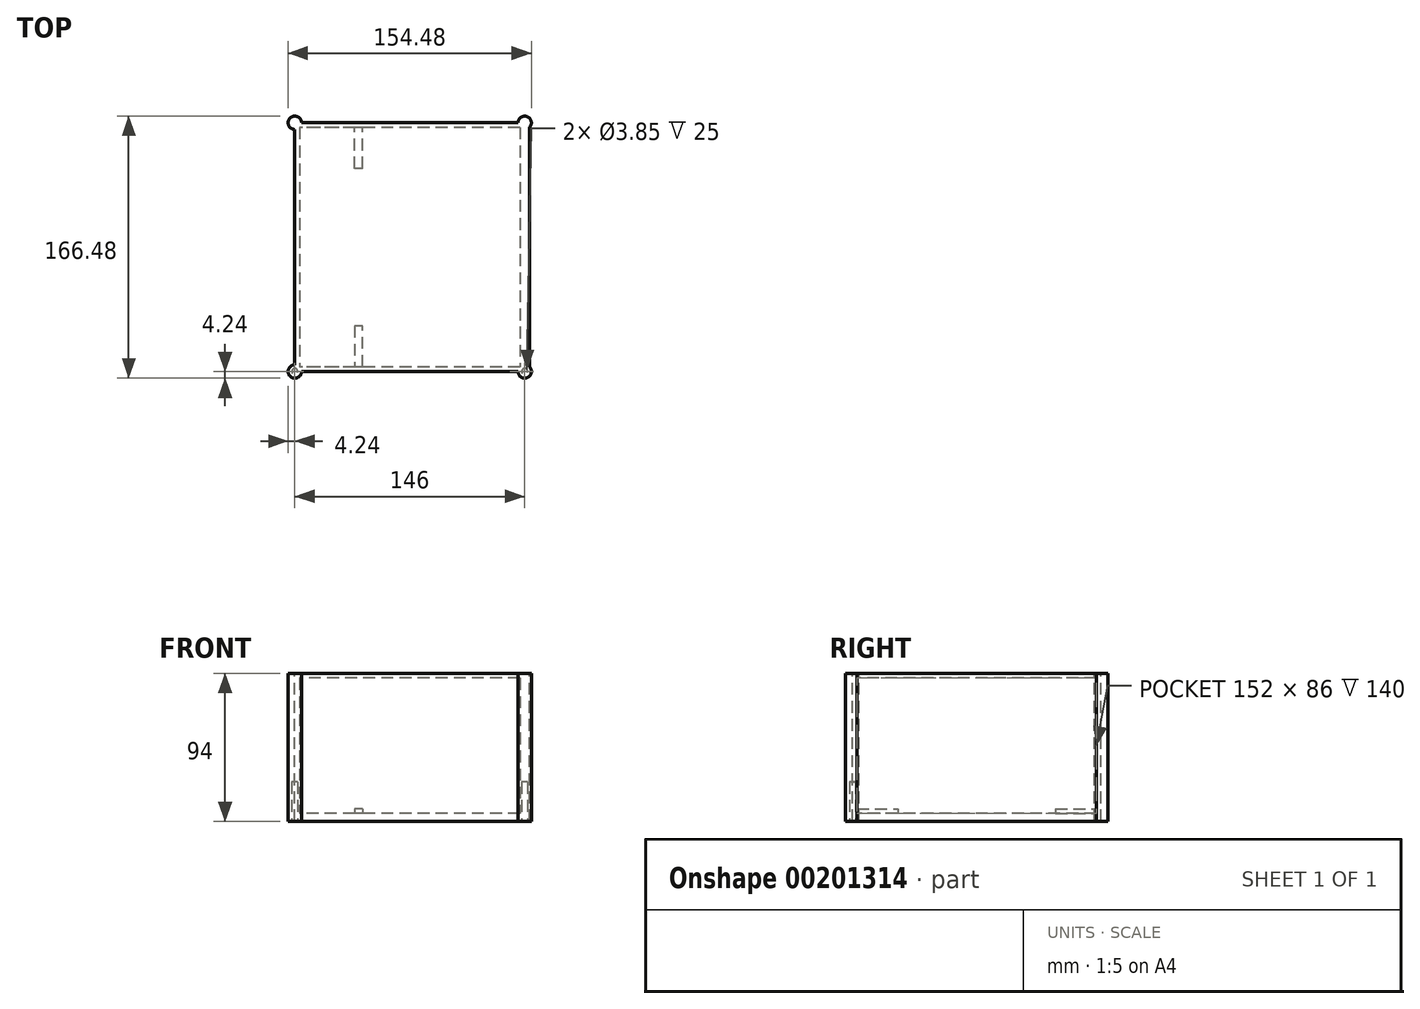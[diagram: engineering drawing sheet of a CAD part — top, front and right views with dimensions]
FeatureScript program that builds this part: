
annotation { "Feature Type Name" : "Feature", "Feature Type Description" : "" }
export const myFeature = defineFeature(function(context is Context, id is Id, definition is map)
    precondition{}
    {
        {
            var Q0;
            Q0=qCreatedBy(makeId("Top.planeOp"),FACE);
            var sketch = newSketch(context, id + "F0", { "sketchPlane" : qUnion([Q0])});
            skLineSegment(sketch, "E0.bottom", {"start": v(70, 76) * mm, "end": v(-70, 76) * mm});
            skLineSegment(sketch, "E0.top", {"start": v(70, -76) * mm, "end": v(-70, -76) * mm});
            skLineSegment(sketch, "E0.left", {"start": v(70, 76) * mm, "end": v(70, -76) * mm});
            skLineSegment(sketch, "E0.right", {"start": v(-70, 76) * mm, "end": v(-70, -76) * mm});
            skPoint(sketch, "E0.middle", {"position": v(0, 0) * mm});
            skLineSegment(sketch, "E1", {"start": v(-30, -76) * mm, "end": v(-30, 76) * mm});
            skLineSegment(sketch, "E2", {"start": v(-30, 50) * mm, "end": v(-35, 50) * mm});
            skLineSegment(sketch, "E3", {"start": v(-35, 50) * mm, "end": v(-35, 76) * mm});
            skLineSegment(sketch, "E4", {"start": v(0, 0) * mm, "end": v(70, 0) * mm, "construction": true});
            skLineSegment(sketch, "E5.MirrorCS", {"start": v(-30, -50) * mm, "end": v(-35, -50) * mm});
            skLineSegment(sketch, "E6.MirrorCS", {"start": v(-35, -50) * mm, "end": v(-35, -76) * mm});
            skLineSegment(sketch, "E7.0", {"start": v(73, 79) * mm, "end": v(73, -79) * mm});
            skLineSegment(sketch, "E7.1", {"start": v(73, 79) * mm, "end": v(-73, 79) * mm});
            skLineSegment(sketch, "E7.2", {"start": v(-73, 79) * mm, "end": v(-73, -79) * mm});
            skLineSegment(sketch, "E7.3", {"start": v(73, -79) * mm, "end": v(-73, -79) * mm});
            skLineSegment(sketch, "E8", {"start": v(70, -76) * mm, "end": v(73, -76) * mm});
            skLineSegment(sketch, "E9", {"start": v(70, 76) * mm, "end": v(73, 76) * mm});
            skCircle(sketch, "E10", {"center": v(73, -79) * mm, "radius": 4.24 * mm});
            skCircle(sketch, "E11", {"center": v(73, 79) * mm, "radius": 4.24 * mm});
            skCircle(sketch, "E12", {"center": v(-73, -79) * mm, "radius": 4.24 * mm});
            skCircle(sketch, "E13.MirrorC", {"center": v(-73, 79) * mm, "radius": 4.24 * mm});
            skSolve(sketch);
        }
        {
            var Q0;
            {var subQ1=sQuery(id+"F0.wireOp",EDGE,"E0.left");Q0=makeQuery(id+"F0.imprint","IMPRINT",FACE,{"disambiguationData":[TD([[makeQuery(id+"F0.imprint","IMPRINT",EDGE,{"derivedFrom":subQ1}),1.0]])]});}
            var Q1;
            {var subQ4=sQuery(id+"F0.wireOp",EDGE,"E0.left");Q1=makeQuery(id+"F0.imprint","IMPRINT",FACE,{"disambiguationData":[TD([[makeQuery(id+"F0.imprint","IMPRINT",EDGE,{"derivedFrom":subQ4}),-1.0]])]});}
            var Q2;
            {var subQ3=sQuery(id+"F0.wireOp",EDGE,"E0.right");Q2=makeQuery(id+"F0.imprint","IMPRINT",FACE,{"disambiguationData":[TD([[makeQuery(id+"F0.imprint","IMPRINT",EDGE,{"derivedFrom":subQ3}),1.0]])]});}
            var Q3;
            {var subQ4=sQuery(id+"F0.wireOp",EDGE,"E5.MirrorCS");Q3=makeQuery(id+"F0.imprint","IMPRINT",FACE,{"disambiguationData":[TD([[makeQuery(id+"F0.imprint","IMPRINT",EDGE,{"derivedFrom":subQ4}),1.0]])]});}
            var Q4;
            {var subQ4=sQuery(id+"F0.wireOp",EDGE,"E2");Q4=makeQuery(id+"F0.imprint","IMPRINT",FACE,{"disambiguationData":[TD([[makeQuery(id+"F0.imprint","IMPRINT",EDGE,{"derivedFrom":subQ4}),-1.0]])]});}
            var Q5;
            {var subQ5=sQuery(id+"F0.wireOp",EDGE,"E0.right");Q5=makeQuery(id+"F0.imprint","IMPRINT",FACE,{"disambiguationData":[TD([[makeQuery(id+"F0.imprint","IMPRINT",EDGE,{"derivedFrom":subQ5}),-1.0]])]});}
            var Q6;
            {var subQ0=sQuery(id+"F0.wireOp",EDGE,"E8");Q6=makeQuery(id+"F0.imprint","IMPRINT",FACE,{"disambiguationData":[TD([[makeQuery(id+"F0.imprint","IMPRINT",EDGE,{"derivedFrom":subQ0}),1.0]])]});}
            var Q7;
            {var subQ3=sQuery(id+"F0.wireOp",EDGE,"E8");Q7=makeQuery(id+"F0.imprint","IMPRINT",FACE,{"disambiguationData":[TD([[makeQuery(id+"F0.imprint","IMPRINT",EDGE,{"derivedFrom":subQ3}),-1.0]])]});}
            var Q8;
            {var subQ0=sQuery(id+"F0.wireOp",EDGE,"E7.0");var subQ1=makeQuery(id+"F0.imprint","INTERSECT",VERTEX,{"derivedFrom":[subQ0,sQuery(id+"F0.wireOp",EDGE,"E8")]});Q8=makeQuery(id+"F0.imprint","IMPRINT",FACE,{"disambiguationData":[TD([[makeQuery(id+"F0.imprint","IMPRINT",EDGE,{"disambiguationData":[TD([[subQ1,1.0]])],"derivedFrom":subQ0}),1.0]])]});}
            var Q9;
            {var subQ0=sQuery(id+"F0.wireOp",EDGE,"E9");Q9=makeQuery(id+"F0.imprint","IMPRINT",FACE,{"disambiguationData":[TD([[makeQuery(id+"F0.imprint","IMPRINT",EDGE,{"derivedFrom":subQ0}),-1.0]])]});}
            var Q10;
            {var subQ3=sQuery(id+"F0.wireOp",EDGE,"E9");Q10=makeQuery(id+"F0.imprint","IMPRINT",FACE,{"disambiguationData":[TD([[makeQuery(id+"F0.imprint","IMPRINT",EDGE,{"derivedFrom":subQ3}),1.0]])]});}
            var Q11;
            {var subQ0=sQuery(id+"F0.wireOp",EDGE,"E7.1");var subQ1=sQuery(id+"F0.wireOp",EDGE,"E7.0");var subQ2=makeQuery(id+"F0.imprint","INTERSECT",VERTEX,{"derivedFrom":[subQ1,subQ0]});Q11=makeQuery(id+"F0.imprint","IMPRINT",FACE,{"disambiguationData":[TD([[makeQuery(id+"F0.imprint","IMPRINT",EDGE,{"disambiguationData":[TD([[subQ2,-1.0]])],"derivedFrom":subQ1}),1.0]])]});}
            var Q12;
            {var subQ0=sQuery(id+"F0.wireOp",EDGE,"E2");Q12=makeQuery(id+"F0.imprint","IMPRINT",FACE,{"disambiguationData":[TD([[makeQuery(id+"F0.imprint","IMPRINT",EDGE,{"derivedFrom":subQ0}),1.0]])]});}
            var Q13;
            {var subQ5=sQuery(id+"F0.wireOp",EDGE,"E0.bottom");var subQ6=makeQuery(id+"F0.imprint","INTERSECT",VERTEX,{"derivedFrom":[subQ5,sQuery(id+"F0.wireOp",EDGE,"E1")]});Q13=makeQuery(id+"F0.imprint","IMPRINT",FACE,{"disambiguationData":[TD([[makeQuery(id+"F0.imprint","IMPRINT",EDGE,{"disambiguationData":[TD([[subQ6,-1.0]])],"derivedFrom":subQ5}),-1.0]])]});}
            var Q14;
            {var subQ0=sQuery(id+"F0.wireOp",EDGE,"E7.2");var subQ1=sQuery(id+"F0.wireOp",EDGE,"E7.1");var subQ2=makeQuery(id+"F0.imprint","INTERSECT",VERTEX,{"derivedFrom":[subQ1,subQ0]});Q14=makeQuery(id+"F0.imprint","IMPRINT",FACE,{"disambiguationData":[TD([[makeQuery(id+"F0.imprint","IMPRINT",EDGE,{"disambiguationData":[TD([[subQ2,1.0]])],"derivedFrom":subQ1}),1.0]])]});}
            var Q15;
            {var subQ0=sQuery(id+"F0.wireOp",EDGE,"E7.2");var subQ1=sQuery(id+"F0.wireOp",EDGE,"E7.1");var subQ2=makeQuery(id+"F0.imprint","INTERSECT",VERTEX,{"derivedFrom":[subQ1,subQ0]});Q15=makeQuery(id+"F0.imprint","IMPRINT",FACE,{"disambiguationData":[TD([[makeQuery(id+"F0.imprint","IMPRINT",EDGE,{"disambiguationData":[TD([[subQ2,1.0]])],"derivedFrom":subQ1}),-1.0]])]});}
            var Q16;
            {var subQ0=sQuery(id+"F0.wireOp",EDGE,"E7.3");var subQ1=sQuery(id+"F0.wireOp",EDGE,"E7.2");var subQ2=makeQuery(id+"F0.imprint","INTERSECT",VERTEX,{"derivedFrom":[subQ1,subQ0]});Q16=makeQuery(id+"F0.imprint","IMPRINT",FACE,{"disambiguationData":[TD([[makeQuery(id+"F0.imprint","IMPRINT",EDGE,{"disambiguationData":[TD([[subQ2,1.0]])],"derivedFrom":subQ1}),1.0]])]});}
            var Q17;
            {var subQ0=sQuery(id+"F0.wireOp",EDGE,"E7.3");var subQ1=sQuery(id+"F0.wireOp",EDGE,"E7.2");var subQ2=makeQuery(id+"F0.imprint","INTERSECT",VERTEX,{"derivedFrom":[subQ1,subQ0]});Q17=makeQuery(id+"F0.imprint","IMPRINT",FACE,{"disambiguationData":[TD([[makeQuery(id+"F0.imprint","IMPRINT",EDGE,{"disambiguationData":[TD([[subQ2,1.0]])],"derivedFrom":subQ1}),-1.0]])]});}
            var Q18;
            {var subQ5=sQuery(id+"F0.wireOp",EDGE,"E0.top");var subQ8=makeQuery(id+"F0.imprint","INTERSECT",VERTEX,{"derivedFrom":[subQ5,sQuery(id+"F0.wireOp",EDGE,"E1")]});Q18=makeQuery(id+"F0.imprint","IMPRINT",FACE,{"disambiguationData":[TD([[makeQuery(id+"F0.imprint","IMPRINT",EDGE,{"disambiguationData":[TD([[subQ8,-1.0]])],"derivedFrom":subQ5}),1.0]])]});}
            extrude(context, id + "F1", {"entities" : qUnion([Q0, Q1, Q2, Q3, Q4, Q5, Q6, Q7, Q8, Q9, Q10, Q11, Q12, Q13, Q14, Q15, Q16, Q17, Q18]), "oppositeDirection" : true, "depth" : 5 * mm});
        }
        {
            var Q0;
            Q0=makeQuery(id+"F0.imprint","IMPRINT",FACE,{"disambiguationData":[TD([[makeQuery(id+"F0.imprint","IMPRINT",EDGE,{"derivedFrom":sQuery(id+"F0.wireOp",EDGE,"E0.left")}),1.0]])]});
            extrude(context, id + "F2", {"entities" : qUnion([Q0]), "operationType" : NewBodyOperationType.ADD, "depth" : 86 * mm});
        }
        {
            var Q0;
            {var subQ4=sQuery(id+"F0.wireOp",EDGE,"E2");Q0=makeQuery(id+"F0.imprint","IMPRINT",FACE,{"disambiguationData":[TD([[makeQuery(id+"F0.imprint","IMPRINT",EDGE,{"derivedFrom":subQ4}),-1.0]])]});}
            var Q1;
            {var subQ4=sQuery(id+"F0.wireOp",EDGE,"E5.MirrorCS");Q1=makeQuery(id+"F0.imprint","IMPRINT",FACE,{"disambiguationData":[TD([[makeQuery(id+"F0.imprint","IMPRINT",EDGE,{"derivedFrom":subQ4}),1.0]])]});}
            extrude(context, id + "F3", {"entities" : qUnion([Q0, Q1]), "operationType" : NewBodyOperationType.ADD, "depth" : 3 * mm});
        }
        {
            var Q0;
            {var subQ5=sQuery(id+"F0.wireOp",EDGE,"E0.right");Q0=makeQuery(id+"F0.imprint","IMPRINT",FACE,{"disambiguationData":[TD([[makeQuery(id+"F0.imprint","IMPRINT",EDGE,{"derivedFrom":subQ5}),-1.0]])]});}
            var Q1;
            {var subQ3=sQuery(id+"F0.wireOp",EDGE,"E8");Q1=makeQuery(id+"F0.imprint","IMPRINT",FACE,{"disambiguationData":[TD([[makeQuery(id+"F0.imprint","IMPRINT",EDGE,{"derivedFrom":subQ3}),-1.0]])]});}
            var Q2;
            {var subQ3=sQuery(id+"F0.wireOp",EDGE,"E9");Q2=makeQuery(id+"F0.imprint","IMPRINT",FACE,{"disambiguationData":[TD([[makeQuery(id+"F0.imprint","IMPRINT",EDGE,{"derivedFrom":subQ3}),1.0]])]});}
            var Q3;
            {var subQ0=sQuery(id+"F0.wireOp",EDGE,"E7.1");var subQ1=sQuery(id+"F0.wireOp",EDGE,"E7.0");var subQ2=makeQuery(id+"F0.imprint","INTERSECT",VERTEX,{"derivedFrom":[subQ1,subQ0]});Q3=makeQuery(id+"F0.imprint","IMPRINT",FACE,{"disambiguationData":[TD([[makeQuery(id+"F0.imprint","IMPRINT",EDGE,{"disambiguationData":[TD([[subQ2,-1.0]])],"derivedFrom":subQ1}),1.0]])]});}
            var Q4;
            {var subQ0=sQuery(id+"F0.wireOp",EDGE,"E7.0");var subQ1=makeQuery(id+"F0.imprint","INTERSECT",VERTEX,{"derivedFrom":[subQ0,sQuery(id+"F0.wireOp",EDGE,"E8")]});Q4=makeQuery(id+"F0.imprint","IMPRINT",FACE,{"disambiguationData":[TD([[makeQuery(id+"F0.imprint","IMPRINT",EDGE,{"disambiguationData":[TD([[subQ1,1.0]])],"derivedFrom":subQ0}),1.0]])]});}
            var Q5;
            {var subQ0=sQuery(id+"F0.wireOp",EDGE,"E8");Q5=makeQuery(id+"F0.imprint","IMPRINT",FACE,{"disambiguationData":[TD([[makeQuery(id+"F0.imprint","IMPRINT",EDGE,{"derivedFrom":subQ0}),1.0]])]});}
            var Q6;
            {var subQ0=sQuery(id+"F0.wireOp",EDGE,"E9");Q6=makeQuery(id+"F0.imprint","IMPRINT",FACE,{"disambiguationData":[TD([[makeQuery(id+"F0.imprint","IMPRINT",EDGE,{"derivedFrom":subQ0}),-1.0]])]});}
            var Q7;
            {var subQ3=sQuery(id+"F0.wireOp",EDGE,"1c2b32d9-a7ae-4baf-86f2-c4eb9871d60d0.MirrorCS");Q7=makeQuery(id+"F0.imprint","IMPRINT",FACE,{"disambiguationData":[TD([[makeQuery(id+"F0.imprint","IMPRINT",EDGE,{"derivedFrom":subQ3}),-1.0]])]});}
            var Q8;
            {var subQ3=sQuery(id+"F0.wireOp",EDGE,"xGjk17qi-ysel-hScp-d5ul-HpHYttQAmUot");Q8=makeQuery(id+"F0.imprint","IMPRINT",FACE,{"disambiguationData":[TD([[makeQuery(id+"F0.imprint","IMPRINT",EDGE,{"derivedFrom":subQ3}),1.0]])]});}
            var Q9;
            {var subQ0=sQuery(id+"F0.wireOp",EDGE,"E7.3");var subQ1=sQuery(id+"F0.wireOp",EDGE,"E7.2");var subQ2=makeQuery(id+"F0.imprint","INTERSECT",VERTEX,{"derivedFrom":[subQ1,subQ0]});Q9=makeQuery(id+"F0.imprint","IMPRINT",FACE,{"disambiguationData":[TD([[makeQuery(id+"F0.imprint","IMPRINT",EDGE,{"disambiguationData":[TD([[subQ2,1.0]])],"derivedFrom":subQ1}),1.0]])]});}
            var Q10;
            {var subQ5=sQuery(id+"F0.wireOp",EDGE,"E0.top");var subQ8=makeQuery(id+"F0.imprint","INTERSECT",VERTEX,{"derivedFrom":[subQ5,sQuery(id+"F0.wireOp",EDGE,"E1")]});Q10=makeQuery(id+"F0.imprint","IMPRINT",FACE,{"disambiguationData":[TD([[makeQuery(id+"F0.imprint","IMPRINT",EDGE,{"disambiguationData":[TD([[subQ8,-1.0]])],"derivedFrom":subQ5}),1.0]])]});}
            var Q11;
            {var subQ0=sQuery(id+"F0.wireOp",EDGE,"E7.3");var subQ1=sQuery(id+"F0.wireOp",EDGE,"E7.2");var subQ2=makeQuery(id+"F0.imprint","INTERSECT",VERTEX,{"derivedFrom":[subQ1,subQ0]});Q11=makeQuery(id+"F0.imprint","IMPRINT",FACE,{"disambiguationData":[TD([[makeQuery(id+"F0.imprint","IMPRINT",EDGE,{"disambiguationData":[TD([[subQ2,1.0]])],"derivedFrom":subQ1}),-1.0]])]});}
            var Q12;
            {var subQ5=sQuery(id+"F0.wireOp",EDGE,"E0.bottom");var subQ6=makeQuery(id+"F0.imprint","INTERSECT",VERTEX,{"derivedFrom":[subQ5,sQuery(id+"F0.wireOp",EDGE,"E1")]});Q12=makeQuery(id+"F0.imprint","IMPRINT",FACE,{"disambiguationData":[TD([[makeQuery(id+"F0.imprint","IMPRINT",EDGE,{"disambiguationData":[TD([[subQ6,-1.0]])],"derivedFrom":subQ5}),-1.0]])]});}
            var Q13;
            {var subQ0=sQuery(id+"F0.wireOp",EDGE,"E7.2");var subQ1=sQuery(id+"F0.wireOp",EDGE,"E7.1");var subQ2=makeQuery(id+"F0.imprint","INTERSECT",VERTEX,{"derivedFrom":[subQ1,subQ0]});Q13=makeQuery(id+"F0.imprint","IMPRINT",FACE,{"disambiguationData":[TD([[makeQuery(id+"F0.imprint","IMPRINT",EDGE,{"disambiguationData":[TD([[subQ2,1.0]])],"derivedFrom":subQ1}),-1.0]])]});}
            var Q14;
            {var subQ0=sQuery(id+"F0.wireOp",EDGE,"E7.2");var subQ1=sQuery(id+"F0.wireOp",EDGE,"E7.1");var subQ2=makeQuery(id+"F0.imprint","INTERSECT",VERTEX,{"derivedFrom":[subQ1,subQ0]});Q14=makeQuery(id+"F0.imprint","IMPRINT",FACE,{"disambiguationData":[TD([[makeQuery(id+"F0.imprint","IMPRINT",EDGE,{"disambiguationData":[TD([[subQ2,1.0]])],"derivedFrom":subQ1}),1.0]])]});}
            extrude(context, id + "F4", {"entities" : qUnion([Q0, Q1, Q2, Q3, Q4, Q5, Q6, Q7, Q8, Q9, Q10, Q11, Q12, Q13, Q14]), "depth" : 89 * mm});
        }
        {
            var Q0;
            {var subQ4=sQuery(id+"F0.wireOp",EDGE,"E0.left");Q0=makeQuery(id+"F0.imprint","IMPRINT",FACE,{"disambiguationData":[TD([[makeQuery(id+"F0.imprint","IMPRINT",EDGE,{"derivedFrom":subQ4}),-1.0]])]});}
            var Q1;
            {var subQ3=sQuery(id+"F0.wireOp",EDGE,"E0.right");Q1=makeQuery(id+"F0.imprint","IMPRINT",FACE,{"disambiguationData":[TD([[makeQuery(id+"F0.imprint","IMPRINT",EDGE,{"derivedFrom":subQ3}),1.0]])]});}
            var Q2;
            {var subQ4=sQuery(id+"F0.wireOp",EDGE,"E2");Q2=makeQuery(id+"F0.imprint","IMPRINT",FACE,{"disambiguationData":[TD([[makeQuery(id+"F0.imprint","IMPRINT",EDGE,{"derivedFrom":subQ4}),-1.0]])]});}
            var Q3;
            {var subQ4=sQuery(id+"F0.wireOp",EDGE,"E5.MirrorCS");Q3=makeQuery(id+"F0.imprint","IMPRINT",FACE,{"disambiguationData":[TD([[makeQuery(id+"F0.imprint","IMPRINT",EDGE,{"derivedFrom":subQ4}),1.0]])]});}
            var Q4;
            Q4=makeQuery(id+"F0.imprint","IMPRINT",FACE,{"disambiguationData":[TD([[makeQuery(id+"F0.imprint","IMPRINT",EDGE,{"derivedFrom":sQuery(id+"F0.wireOp",EDGE,"E0.left")}),1.0]])]});
            var Q5;
            {var subQ0=sQuery(id+"F0.wireOp",EDGE,"E8");Q5=makeQuery(id+"F0.imprint","IMPRINT",FACE,{"disambiguationData":[TD([[makeQuery(id+"F0.imprint","IMPRINT",EDGE,{"derivedFrom":subQ0}),1.0]])]});}
            var Q6;
            {var subQ0=sQuery(id+"F0.wireOp",EDGE,"E9");Q6=makeQuery(id+"F0.imprint","IMPRINT",FACE,{"disambiguationData":[TD([[makeQuery(id+"F0.imprint","IMPRINT",EDGE,{"derivedFrom":subQ0}),-1.0]])]});}
            var Q7;
            {var subQ3=sQuery(id+"F0.wireOp",EDGE,"E9");Q7=makeQuery(id+"F0.imprint","IMPRINT",FACE,{"disambiguationData":[TD([[makeQuery(id+"F0.imprint","IMPRINT",EDGE,{"derivedFrom":subQ3}),1.0]])]});}
            var Q8;
            {var subQ4=sQuery(id+"F0.wireOp",EDGE,"E0.right");Q8=makeQuery(id+"F0.imprint","IMPRINT",FACE,{"disambiguationData":[TD([[makeQuery(id+"F0.imprint","IMPRINT",EDGE,{"derivedFrom":subQ4}),-1.0]])]});}
            var Q9;
            {var subQ0=sQuery(id+"F0.wireOp",EDGE,"E7.1");var subQ1=sQuery(id+"F0.wireOp",EDGE,"E7.0");var subQ2=makeQuery(id+"F0.imprint","INTERSECT",VERTEX,{"derivedFrom":[subQ1,subQ0]});Q9=makeQuery(id+"F0.imprint","IMPRINT",FACE,{"disambiguationData":[TD([[makeQuery(id+"F0.imprint","IMPRINT",EDGE,{"disambiguationData":[TD([[subQ2,-1.0]])],"derivedFrom":subQ1}),1.0]])]});}
            var Q10;
            {var subQ3=sQuery(id+"F0.wireOp",EDGE,"E8");Q10=makeQuery(id+"F0.imprint","IMPRINT",FACE,{"disambiguationData":[TD([[makeQuery(id+"F0.imprint","IMPRINT",EDGE,{"derivedFrom":subQ3}),-1.0]])]});}
            var Q11;
            {var subQ0=sQuery(id+"F0.wireOp",EDGE,"E7.0");var subQ1=makeQuery(id+"F0.imprint","INTERSECT",VERTEX,{"derivedFrom":[subQ0,sQuery(id+"F0.wireOp",EDGE,"E8")]});Q11=makeQuery(id+"F0.imprint","IMPRINT",FACE,{"disambiguationData":[TD([[makeQuery(id+"F0.imprint","IMPRINT",EDGE,{"disambiguationData":[TD([[subQ1,1.0]])],"derivedFrom":subQ0}),1.0]])]});}
            var Q12;
            {var subQ0=sQuery(id+"F0.wireOp",EDGE,"E2");Q12=makeQuery(id+"F0.imprint","IMPRINT",FACE,{"disambiguationData":[TD([[makeQuery(id+"F0.imprint","IMPRINT",EDGE,{"derivedFrom":subQ0}),1.0]])]});}
            extrude(context, id + "F5", {"entities" : qUnion([Q0, Q1, Q2, Q3, Q4, Q5, Q6, Q7, Q8, Q9, Q10, Q11, Q12]), "operationType" : NewBodyOperationType.ADD, "depth" : 89 * mm, "hasSecondDirection" : true, "secondDirectionOppositeDirection" : false, "secondDirectionDepth" : 86 * mm});
        }
        {
            var Q0;
            Q0=qCreatedBy(makeId("Top.planeOp"),FACE);
            var sketch = newSketch(context, id + "F6", { "sketchPlane" : qUnion([Q0])});
            skCircle(sketch, "E14", {"center": v(73, -79) * mm, "radius": 1.93 * mm});
            skCircle(sketch, "E15.MirrorC", {"center": v(73, 79) * mm, "radius": 1.93 * mm});
            skCircle(sketch, "E16", {"center": v(-73, -79) * mm, "radius": 1.93 * mm});
            skCircle(sketch, "E17.MirrorC", {"center": v(-73, 79) * mm, "radius": 1.93 * mm});
            skSolve(sketch);
        }
        {
            var Q0;
            Q0=makeQuery(id+"F6.imprint","IMPRINT",FACE,{"disambiguationData":[TD([[makeQuery(id+"F6.imprint","IMPRINT",EDGE,{"derivedFrom":sQuery(id+"F6.wireOp",EDGE,"E14")}),1.0]])]});
            var Q1;
            Q1=makeQuery(id+"F6.imprint","IMPRINT",FACE,{"disambiguationData":[TD([[makeQuery(id+"F6.imprint","IMPRINT",EDGE,{"derivedFrom":sQuery(id+"F6.wireOp",EDGE,"E15.MirrorC")}),-1.0]])]});
            var Q2;
            Q2=makeQuery(id+"F6.imprint","IMPRINT",FACE,{"disambiguationData":[TD([[makeQuery(id+"F6.imprint","IMPRINT",EDGE,{"derivedFrom":sQuery(id+"F6.wireOp",EDGE,"E16")}),1.0]])]});
            var Q3;
            Q3=makeQuery(id+"F6.imprint","IMPRINT",FACE,{"disambiguationData":[TD([[makeQuery(id+"F6.imprint","IMPRINT",EDGE,{"derivedFrom":sQuery(id+"F6.wireOp",EDGE,"E17.MirrorC")}),-1.0]])]});
            extrude(context, id + "F7", {"entities" : qUnion([Q0, Q1, Q2, Q3]), "operationType" : NewBodyOperationType.REMOVE, "depth" : 20 * mm, "hasSecondDirection" : true, "secondDirectionOppositeDirection" : true, "secondDirectionDepth" : 5 * mm});
        }
        {
            var Q0;
            Q0=makeQuery(id+"F5.opExtrude","SWEPT_FACE",FACE,{"disambiguationData":[OSD([sQuery(id+"F0.wireOp",EDGE,"E7.0")])]});
            extrude(context, id + "F8", {"entities" : qUnion([Q0]), "operationType" : NewBodyOperationType.ADD, "depth" : 3 * mm});
        }
        {
            var Q0;
            Q0=makeQuery(id+"F8.opExtrude","SWEPT_FACE",FACE,{"disambiguationData":[OSD([sQuery(id+"F0.wireOp",EDGE,"E7.0"),sQuery(id+"F0.wireOp",EDGE,"E10")])]});
            extrude(context, id + "F9", {"entities" : qUnion([Q0]), "operationType" : NewBodyOperationType.ADD, "endBound" : BoundingType.UP_TO_NEXT, "depth" : 25 * mm});
        }
        {
            var Q0;
            Q0=makeQuery(id+"F8.opExtrude","SWEPT_FACE",FACE,{"disambiguationData":[OSD([sQuery(id+"F0.wireOp",EDGE,"E7.0"),sQuery(id+"F0.wireOp",EDGE,"E11")])]});
            extrude(context, id + "F10", {"entities" : qUnion([Q0]), "operationType" : NewBodyOperationType.ADD, "endBound" : BoundingType.UP_TO_NEXT, "depth" : 25 * mm});
        }
    });
